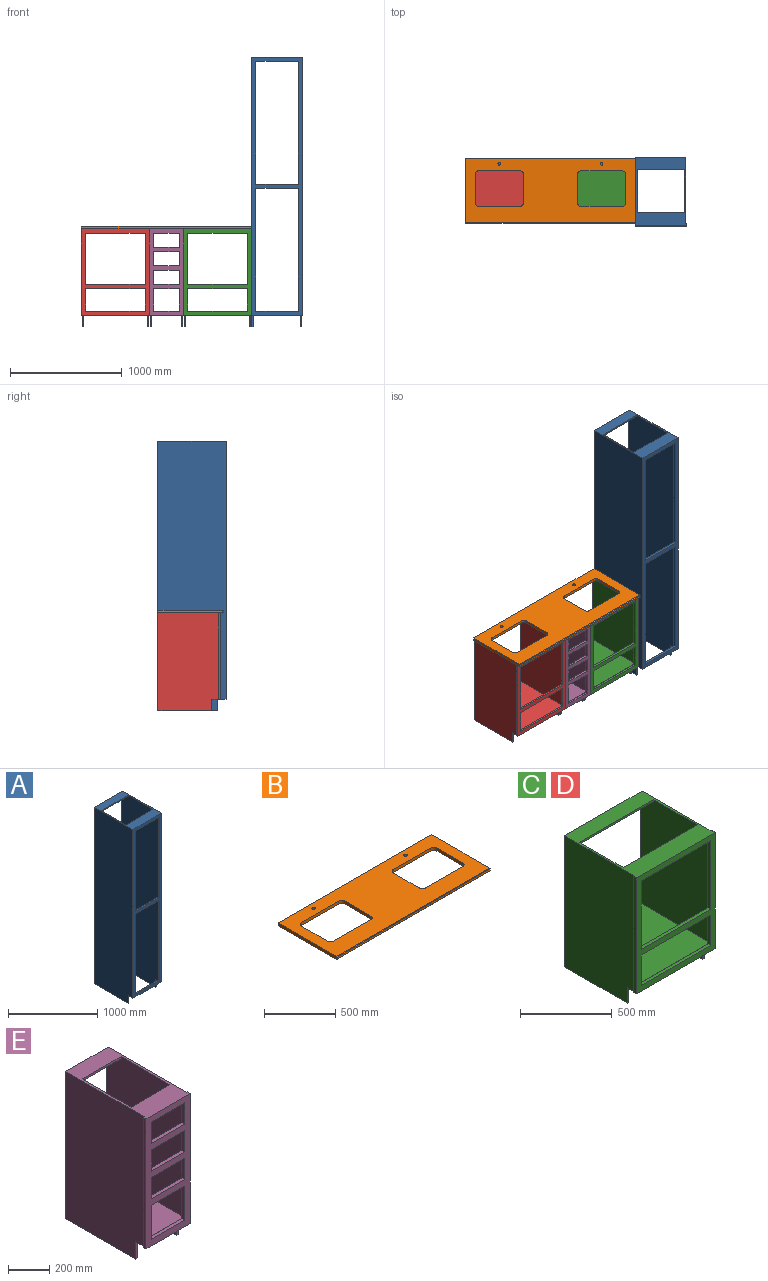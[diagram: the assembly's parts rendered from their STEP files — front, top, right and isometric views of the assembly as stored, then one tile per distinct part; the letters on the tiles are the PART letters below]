
ASSEMBLY  parts=5 mates=6
PART A: 27 faces, bbox 457.2x609.6x2413 mm
  f0: plane 1098.55x19.05mm, normal (1,0,0), area 20927.4mm2, adj f5,f9,f14,f25
  f1: plane 1098.55x19.05mm, normal (-1,0,0), area 20927.4mm2, adj f5,f9,f14,f25
  f2: plane 2413x590.55mm, normal (-1,0,0), area 1416610.1mm2, adj f5,f10,f12,f16,f18,f19,f20,f21
  f3: plane 2413x609.6mm, normal (-1,0,0), area 1463222.9mm2, adj f10,f12,f14,f15,f16,f23
  f4: plane 2413x590.55mm, normal (1,0,0), area 1416610.1mm2, adj f5,f10,f12,f15,f16,f19,f20,f21
  f5: plane 2298.7x425.45mm, normal (0,1,0), area 140886.8mm2, adj f0,f1,f2,f4,f7,f8,f9,f10
  f6: plane 2311.4x6.35mm, normal (0,1,0), area 14677.4mm2, adj f10,f11,f12,f17
  f7: plane 381x19.05mm, normal (0,0,1), area 7258.1mm2, adj f5,f8,f13,f14
  f8: plane 1098.55x19.05mm, normal (1,0,0), area 20927.4mm2, adj f5,f7,f14,f26
  f9: plane 381x19.05mm, normal (0,0,-1), area 7258.1mm2, adj f0,f1,f5,f14
  f10: plane 457.2x76.2mm, normal (0,0,-1), area 10161.3mm2, adj f2,f3,f4,f5,f6,f11,f14,f17
  f11: plane 2311.4x19.05mm, normal (1,0,0), area 44032.2mm2, adj f6,f10,f12,f14
  f12: plane 609.6x457.2mm, normal (0,0,1), area 110161.1mm2, adj f2,f3,f4,f6,f11,f14,f16,f17
  f13: plane 1098.55x19.05mm, normal (-1,0,0), area 20927.4mm2, adj f5,f7,f14,f26
  f14: plane 2311.4x457.2mm, normal (0,-1,0), area 219677mm2, adj f0,f1,f3,f7,f8,f9,f10,f11
  f15: plane 533.4x12.7mm, normal (0,0,-1), area 6774.2mm2, adj f3,f4,f16,f23
  f16: plane 2413x450.85mm, normal (0,1,0), area 66693.4mm2, adj f2,f3,f4,f12,f15,f17,f18,f21
  f17: plane 2413x590.55mm, normal (1,0,0), area 1419190.7mm2, adj f6,f10,f12,f16,f18,f24
  f18: plane 533.4x12.7mm, normal (0,0,-1), area 6774.2mm2, adj f2,f16,f17,f24
  f19: plane 425.45x12.7mm, normal (0,1,0), area 5403.2mm2, adj f2,f4,f12,f20
  f20: plane 425.45x101.6mm, normal (0,0,-1), area 43225.7mm2, adj f2,f4,f5,f19
  f21: plane 425.45x101.6mm, normal (0,0,-1), area 43225.7mm2, adj f2,f4,f16,f22
  f22: plane 425.45x12.7mm, normal (0,-1,0), area 5403.2mm2, adj f2,f4,f12,f21
  f23: plane 101.6x12.7mm, normal (0,-1,0), area 1290.3mm2, adj f3,f4,f10,f15
  f24: plane 101.6x12.7mm, normal (0,-1,0), area 1290.3mm2, adj f2,f10,f17,f18
  f25: plane 381x19.05mm, normal (0,0,1), area 7258.1mm2, adj f0,f1,f5,f14
  f26: plane 381x19.05mm, normal (0,0,-1), area 7258.1mm2, adj f5,f8,f13,f14
PART B: 27 faces, bbox 1524x584.2x25.4 mm
  f0: plane 1524x579.44mm, normal (0,0,1), area 608216mm2, adj f2,f3,f4,f6,f9,f10,f11,f12
  f1: plane 1524x579.44mm, normal (0,0,-1), area 608216mm2, adj f2,f3,f4,f7,f9,f10,f11,f12
  f2: plane 584.2x25.4mm, normal (1,0,0), area 14828.9mm2, adj f0,f1,f3,f5,f6,f7
  f3: plane 1524x25.4mm, normal (0,1,0), area 38709.6mm2, adj f0,f1,f2,f4
  f4: plane 579.44x25.4mm, normal (-1,0,0), area 14717.7mm2, adj f0,f1,f3,f8
  f5: plane 1519.24x15.88mm, normal (0,-1,0), area 24117.9mm2, adj f2,f6,f7,f8
  f6: cylinder r=4.76mm len=1524mm, axis (-1,0,0), area 11388mm2, adj f0,f2,f5,f8
  f7: cylinder r=4.76mm len=1524mm, axis (1,0,0), area 11388mm2, adj f1,f2,f5,f8
  f8: cylinder r=4.76mm len=25.4mm, axis (0,0,1), area 164.1mm2, adj f4,f5,f6,f7
  f9: plane 368.3x25.4mm, normal (0,-1,0), area 9354.8mm2, adj f0,f1,f23,f26
  f10: plane 255.59x25.4mm, normal (1,0,0), area 6491.9mm2, adj f0,f1,f25,f26
  f11: plane 368.3x25.4mm, normal (0,1,0), area 9354.8mm2, adj f0,f1,f24,f25
  f12: plane 255.59x25.4mm, normal (-1,0,0), area 6491.9mm2, adj f0,f1,f23,f24
  f13: plane 368.3x25.4mm, normal (0,-1,0), area 9354.8mm2, adj f0,f1,f19,f22
  f14: plane 255.59x25.4mm, normal (1,0,0), area 6491.9mm2, adj f0,f1,f19,f20
  f15: plane 368.3x25.4mm, normal (0,1,0), area 9354.8mm2, adj f0,f1,f20,f21
  f16: plane 255.59x25.4mm, normal (-1,0,0), area 6491.9mm2, adj f0,f1,f21,f22
  f17: cylinder r=12.7mm len=25.4mm, axis (0,0,1), area 2026.8mm2, adj f0,f1
  f18: cylinder r=12.7mm len=25.4mm, axis (0,0,1), area 2026.8mm2, adj f0,f1
  f19: cylinder r=31.75mm len=31.75mm, axis (0,0,1), area 1266.8mm2, adj f0,f1,f13,f14
  f20: cylinder r=31.75mm len=31.75mm, axis (0,0,-1), area 1266.8mm2, adj f0,f1,f14,f15
  f21: cylinder r=31.75mm len=31.75mm, axis (0,0,1), area 1266.8mm2, adj f0,f1,f15,f16
  f22: cylinder r=31.75mm len=31.75mm, axis (0,0,-1), area 1266.8mm2, adj f0,f1,f13,f16
  f23: cylinder r=31.75mm len=31.75mm, axis (0,0,-1), area 1266.8mm2, adj f0,f1,f9,f12
  f24: cylinder r=31.75mm len=31.75mm, axis (0,0,1), area 1266.8mm2, adj f0,f1,f11,f12
  f25: cylinder r=31.75mm len=31.75mm, axis (0,0,-1), area 1266.8mm2, adj f0,f1,f10,f11
  f26: cylinder r=31.75mm len=31.75mm, axis (0,0,1), area 1266.8mm2, adj f0,f1,f9,f10
PART C: 34 faces, bbox 609.6x558.8x876.3 mm
  f0: plane 457.2x19.05mm, normal (1,0,0), area 8709.7mm2, adj f6,f12,f18,f32
  f1: plane 457.2x19.05mm, normal (-1,0,0), area 8709.7mm2, adj f6,f12,f18,f32
  f2: plane 876.3x539.75mm, normal (-1,0,0), area 467176.5mm2, adj f9,f13,f15,f19,f25,f31
  f3: plane 539.75x123.83mm, normal (1,0,0), area 61028.1mm2, adj f7,f13,f19,f20,f25,f31
  f4: plane 539.75x123.83mm, normal (-1,0,0), area 61028.1mm2, adj f7,f13,f20,f21,f25,f30
  f5: plane 739.78x539.75mm, normal (-1,0,0), area 396712.9mm2, adj f6,f15,f23,f25,f26,f27,f28,f29
  f6: plane 727.08x571.5mm, normal (0,1,0), area 63266mm2, adj f0,f1,f5,f10,f11,f12,f17,f23
  f7: plane 571.5x22.23mm, normal (0,1,0), area 12701.6mm2, adj f3,f4,f13,f20
  f8: plane 774.7x6.35mm, normal (0,1,0), area 4919.3mm2, adj f13,f14,f15,f22
  f9: plane 774.7x6.35mm, normal (0,1,0), area 4919.3mm2, adj f2,f13,f15,f16
  f10: plane 533.4x19.05mm, normal (0,0,1), area 10161.3mm2, adj f6,f11,f17,f18
  f11: plane 203.2x19.05mm, normal (1,0,0), area 3871mm2, adj f6,f10,f18,f33
  f12: plane 533.4x19.05mm, normal (0,0,-1), area 10161.3mm2, adj f0,f1,f6,f18
  f13: plane 609.6x76.2mm, normal (0,0,-1), area 13064.5mm2, adj f2,f3,f4,f7,f8,f9,f14,f16
  f14: plane 774.7x19.05mm, normal (1,0,0), area 14758mm2, adj f8,f13,f15,f18
  f15: plane 609.6x558.8mm, normal (0,0,1), area 141451.3mm2, adj f2,f5,f8,f9,f14,f16,f18,f22
  f16: plane 774.7x19.05mm, normal (-1,0,0), area 14758mm2, adj f9,f13,f15,f18
  f17: plane 203.2x19.05mm, normal (-1,0,0), area 3871mm2, adj f6,f10,f18,f33
  f18: plane 774.7x609.6mm, normal (0,-1,0), area 119999.8mm2, adj f0,f1,f10,f11,f12,f13,f14,f15
  f19: plane 482.6x12.7mm, normal (0,0,-1), area 6129mm2, adj f2,f3,f25,f31
  f20: plane 571.5x539.75mm, normal (0,0,-1), area 308467.1mm2, adj f3,f4,f7,f25
  f21: plane 482.6x12.7mm, normal (0,0,-1), area 6129mm2, adj f4,f22,f25,f30
  f22: plane 876.3x539.75mm, normal (1,0,0), area 467176.5mm2, adj f8,f13,f15,f21,f25,f30
  f23: plane 571.5x539.75mm, normal (0,0,1), area 308467.1mm2, adj f5,f6,f24,f25
  f24: plane 739.78x539.75mm, normal (1,0,0), area 396712.9mm2, adj f6,f15,f23,f25,f26,f27,f28,f29
  f25: plane 876.3x596.9mm, normal (0,1,0), area 36774.1mm2, adj f2,f3,f4,f5,f15,f19,f20,f21
  f26: plane 571.5x12.7mm, normal (0,1,0), area 7258mm2, adj f5,f15,f24,f27
  f27: plane 571.5x101.6mm, normal (0,0,-1), area 58064.4mm2, adj f5,f6,f24,f26
  f28: plane 571.5x101.6mm, normal (0,0,-1), area 58064.4mm2, adj f5,f24,f25,f29
  f29: plane 571.5x12.7mm, normal (0,-1,0), area 7258mm2, adj f5,f15,f24,f28
  f30: plane 101.6x12.7mm, normal (0,-1,0), area 1290.3mm2, adj f4,f13,f21,f22
  f31: plane 101.6x12.7mm, normal (0,-1,0), area 1290.3mm2, adj f2,f3,f13,f19
  f32: plane 533.4x19.05mm, normal (0,0,1), area 10161.3mm2, adj f0,f1,f6,f18
  f33: plane 533.4x19.05mm, normal (0,0,-1), area 10161.3mm2, adj f6,f11,f17,f18
PART D: same geometry as C
PART E: 42 faces, bbox 304.8x558.8x876.3 mm
  f0: plane 127x19.05mm, normal (1,0,0), area 2419.3mm2, adj f10,f22,f39,f40
  f1: plane 127x19.05mm, normal (-1,0,0), area 2419.3mm2, adj f10,f22,f39,f40
  f2: plane 127x19.05mm, normal (1,0,0), area 2419.3mm2, adj f10,f22,f37,f38
  f3: plane 127x19.05mm, normal (-1,0,0), area 2419.3mm2, adj f10,f22,f37,f38
  f4: plane 127x19.05mm, normal (1,0,0), area 2419.3mm2, adj f10,f16,f22,f36
  f5: plane 127x19.05mm, normal (-1,0,0), area 2419.3mm2, adj f10,f16,f22,f36
  f6: plane 876.3x539.75mm, normal (-1,0,0), area 467176.5mm2, adj f13,f17,f19,f23,f29,f35
  f7: plane 539.75x123.83mm, normal (1,0,0), area 61028.1mm2, adj f11,f17,f23,f24,f29,f35
  f8: plane 539.75x123.83mm, normal (-1,0,0), area 61028.1mm2, adj f11,f17,f24,f25,f29,f34
  f9: plane 739.78x539.75mm, normal (-1,0,0), area 396712.9mm2, adj f10,f19,f27,f29,f30,f31,f32,f33
  f10: plane 727.08x266.7mm, normal (0,1,0), area 60362.8mm2, adj f0,f1,f2,f3,f4,f5,f9,f14
  f11: plane 266.7x22.23mm, normal (0,1,0), area 5927.4mm2, adj f7,f8,f17,f24
  f12: plane 774.7x6.35mm, normal (0,1,0), area 4919.3mm2, adj f17,f18,f19,f26
  f13: plane 774.7x6.35mm, normal (0,1,0), area 4919.3mm2, adj f6,f17,f19,f20
  f14: plane 228.6x19.05mm, normal (0,0,1), area 4354.8mm2, adj f10,f15,f21,f22
  f15: plane 203.2x19.05mm, normal (1,0,0), area 3871mm2, adj f10,f14,f22,f41
  f16: plane 228.6x19.05mm, normal (0,0,-1), area 4354.8mm2, adj f4,f5,f10,f22
  f17: plane 304.8x76.2mm, normal (0,0,-1), area 7258.1mm2, adj f6,f7,f8,f11,f12,f13,f18,f20
  f18: plane 774.7x19.05mm, normal (1,0,0), area 14758mm2, adj f12,f17,f19,f22
  f19: plane 558.8x304.8mm, normal (0,0,1), area 73709.5mm2, adj f6,f9,f12,f13,f18,f20,f22,f26
  f20: plane 774.7x19.05mm, normal (-1,0,0), area 14758mm2, adj f13,f17,f19,f22
  f21: plane 203.2x19.05mm, normal (-1,0,0), area 3871mm2, adj f10,f14,f22,f41
  f22: plane 774.7x304.8mm, normal (0,-1,0), area 102580.4mm2, adj f0,f1,f2,f3,f4,f5,f14,f15
  f23: plane 482.6x12.7mm, normal (0,0,-1), area 6129mm2, adj f6,f7,f29,f35
  f24: plane 539.75x266.7mm, normal (0,0,-1), area 143951.3mm2, adj f7,f8,f11,f29
  f25: plane 482.6x12.7mm, normal (0,0,-1), area 6129mm2, adj f8,f26,f29,f34
  f26: plane 876.3x539.75mm, normal (1,0,0), area 467176.5mm2, adj f12,f17,f19,f25,f29,f34
  f27: plane 539.75x266.7mm, normal (0,0,1), area 143951.3mm2, adj f9,f10,f28,f29
  f28: plane 739.78x539.75mm, normal (1,0,0), area 396712.9mm2, adj f10,f19,f27,f29,f30,f31,f32,f33
  f29: plane 876.3x292.1mm, normal (0,1,0), area 29032.2mm2, adj f6,f7,f8,f9,f19,f23,f24,f25
  f30: plane 266.7x12.7mm, normal (0,1,0), area 3387.1mm2, adj f9,f19,f28,f31
  f31: plane 266.7x101.6mm, normal (0,0,-1), area 27096.7mm2, adj f9,f10,f28,f30
  f32: plane 266.7x101.6mm, normal (0,0,-1), area 27096.7mm2, adj f9,f28,f29,f33
  f33: plane 266.7x12.7mm, normal (0,-1,0), area 3387.1mm2, adj f9,f19,f28,f32
  f34: plane 101.6x12.7mm, normal (0,-1,0), area 1290.3mm2, adj f8,f17,f25,f26
  f35: plane 101.6x12.7mm, normal (0,-1,0), area 1290.3mm2, adj f6,f7,f17,f23
  f36: plane 228.6x19.05mm, normal (0,0,1), area 4354.8mm2, adj f4,f5,f10,f22
  f37: plane 228.6x19.05mm, normal (0,0,-1), area 4354.8mm2, adj f2,f3,f10,f22
  f38: plane 228.6x19.05mm, normal (0,0,1), area 4354.8mm2, adj f2,f3,f10,f22
  f39: plane 228.6x19.05mm, normal (0,0,-1), area 4354.8mm2, adj f0,f1,f10,f22
  f40: plane 228.6x19.05mm, normal (0,0,1), area 4354.8mm2, adj f0,f1,f10,f22
  f41: plane 228.6x19.05mm, normal (0,0,-1), area 4354.8mm2, adj f10,f15,f21,f22
PLACE A t=(1371.6,-50.8,0)mm
PLACE B t=(914.4,539.75,876.3)mm
PLACE C t=(914.4,0,0)mm
PLACE D at identity fixed
PLACE E t=(304.8,0,0)mm
MATE fastened B.f3 <-> C.f25  axis (0,1,0) through (914.4,539.75,876.3)mm
MATE planar C.f21 <-> A.f15  axis (0,0,-1) through (901.7,298.45,0)mm
MATE planar C.f14 <-> A.f3  axis (1,0,0) through (914.4,-9.53,488.95)mm
MATE fastened E.f17 <-> C.f13  axis (0,0,-1) through (304.8,-19.05,101.6)mm
MATE fastened D.f13 <-> E.f17  axis (0,0,-1) through (0,-19.05,101.6)mm
MATE planar A.f16 <-> C.f25  axis (0,1,0) through (914.4,539.75,0)mm
